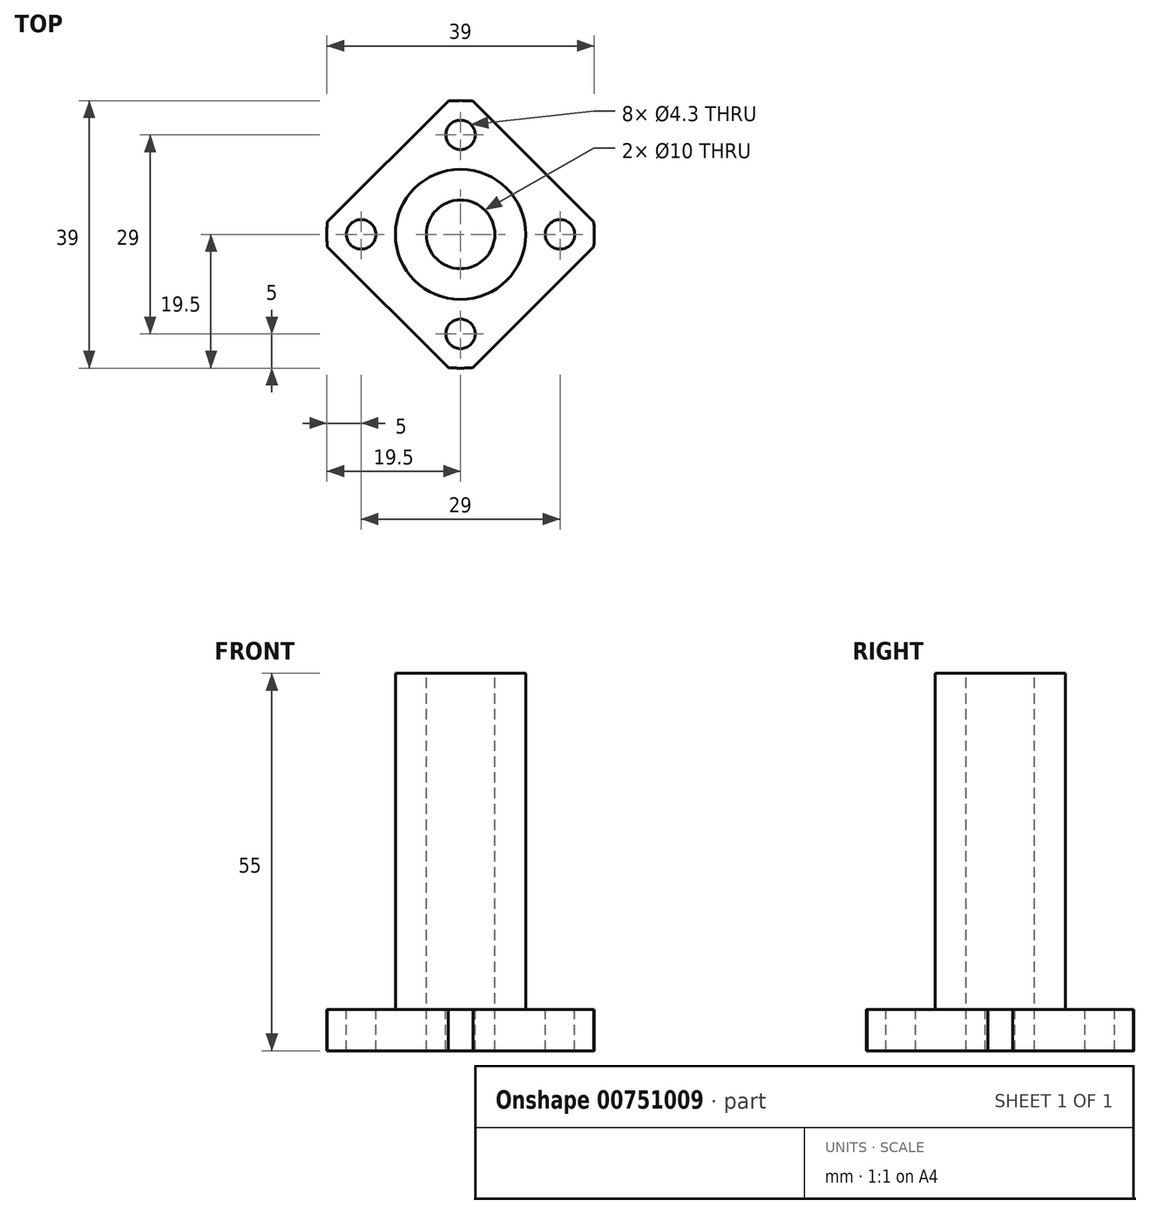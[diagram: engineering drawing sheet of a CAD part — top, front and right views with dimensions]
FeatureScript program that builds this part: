
annotation { "Feature Type Name" : "Feature", "Feature Type Description" : "" }
export const myFeature = defineFeature(function(context is Context, id is Id, definition is map)
    precondition{}
    {
        {
            var Q0;
            Q0=qCreatedBy(makeId("Top.planeOp"),FACE);
            var sketch = newSketch(context, id + "F0", { "sketchPlane" : qUnion([Q0])});
            skCircle(sketch, "E0", {"center": v(0, 0) * mm, "radius": 19.5 * mm});
            skSolve(sketch);
        }
        {
            var Q0;
            Q0=qSketchRegion(id+"F0",true);
            extrude(context, id + "F1", {"entities" : qUnion([Q0]), "depth" : 6 * mm});
        }
        {
            var Q0;
            Q0=makeQuery(id+"F1.opExtrude","CAP_FACE",FACE,{"disambiguationData":[OSD([sQuery(id+"F0.wireOp",EDGE,"E0")])],"isStart":false});
            var sketch = newSketch(context, id + "F2", { "sketchPlane" : qUnion([Q0])});
            skCircle(sketch, "E1", {"center": v(0, 0) * mm, "radius": 9.5 * mm});
            skSolve(sketch);
        }
        {
            var Q0;
            Q0=qSketchRegion(id+"F2",true);
            extrude(context, id + "F3", {"entities" : qUnion([Q0]), "operationType" : NewBodyOperationType.ADD, "depth" : (55 - 6) * mm});
        }
        {
            var Q0;
            Q0=makeQuery(id+"F3.opExtrude","CAP_FACE",FACE,{"disambiguationData":[OSD([sQuery(id+"F2.wireOp",EDGE,"E1")])],"isStart":false});
            var sketch = newSketch(context, id + "F4", { "sketchPlane" : qUnion([Q0])});
            skCircle(sketch, "E2", {"center": v(0, 0) * mm, "radius": 5 * mm});
            skSolve(sketch);
        }
        {
            var Q0;
            Q0=qSketchRegion(id+"F4",true);
            extrude(context, id + "F5", {"entities" : qUnion([Q0]), "operationType" : NewBodyOperationType.REMOVE, "endBound" : BoundingType.THROUGH_ALL, "oppositeDirection" : true, "depth" : 25 * mm});
        }
        {
            var Q0;
            Q0=makeQuery(id+"F1.opExtrude","CAP_FACE",FACE,{"disambiguationData":[OSD([sQuery(id+"F0.wireOp",EDGE,"E0")])],"isStart":false});
            var sketch = newSketch(context, id + "F6", { "sketchPlane" : qUnion([Q0])});
            skCircle(sketch, "E3", {"center": v(0, 14.5) * mm, "radius": 2.15 * mm});
            skCircle(sketch, "E4.1.0", {"center": v(-14.5, 0) * mm, "radius": 2.15 * mm});
            skCircle(sketch, "E4.2.0", {"center": v(0, -14.5) * mm, "radius": 2.15 * mm});
            skCircle(sketch, "E4.3.0", {"center": v(14.5, 0) * mm, "radius": 2.15 * mm});
            skPoint(sketch, "E4.center", {"position": v(0, 0) * mm});
            skSolve(sketch);
        }
        {
            var Q0;
            Q0=qSketchRegion(id+"F6",true);
            extrude(context, id + "F7", {"entities" : qUnion([Q0]), "operationType" : NewBodyOperationType.REMOVE, "oppositeDirection" : true, "depth" : 25 * mm});
        }
        {
            var Q0;
            Q0=makeQuery(id+"F1.opExtrude","SWEPT_BODY",BODY,{"disambiguationData":[OSD([sQuery(id+"F0.wireOp",EDGE,"E0")])]});
            transform(context, id + "F8", {"entities" : qUnion([Q0]), "transformType" : TransformType.COPY});
        }
        {
            var Q0;
            Q0=qCreatedBy(makeId("Top.planeOp"),FACE);
            var sketch = newSketch(context, id + "F9", { "sketchPlane" : qUnion([Q0])});
            skLineSegment(sketch, "E5.bottom", {"start": v(21.21, 0) * mm, "end": v(0, 21.21) * mm});
            skLineSegment(sketch, "E5.top", {"start": v(0, -21.21) * mm, "end": v(-21.21, 0) * mm});
            skLineSegment(sketch, "E5.left", {"start": v(21.21, 0) * mm, "end": v(0, -21.21) * mm});
            skLineSegment(sketch, "E5.right", {"start": v(0, 21.21) * mm, "end": v(-21.21, 0) * mm});
            skPoint(sketch, "E5.middle", {"position": v(0, 0) * mm});
            skLineSegment(sketch, "E6", {"start": v(0, 33.66) * mm, "end": v(0, 28.47) * mm, "construction": true});
            skSolve(sketch);
        }
        {
            var Q0;
            Q0=qSketchRegion(id+"F9",true);
            extrude(context, id + "F10", {"entities" : qUnion([Q0]), "operationType" : NewBodyOperationType.INTERSECT, "depth" : 59.2 * mm});
        }
    });
